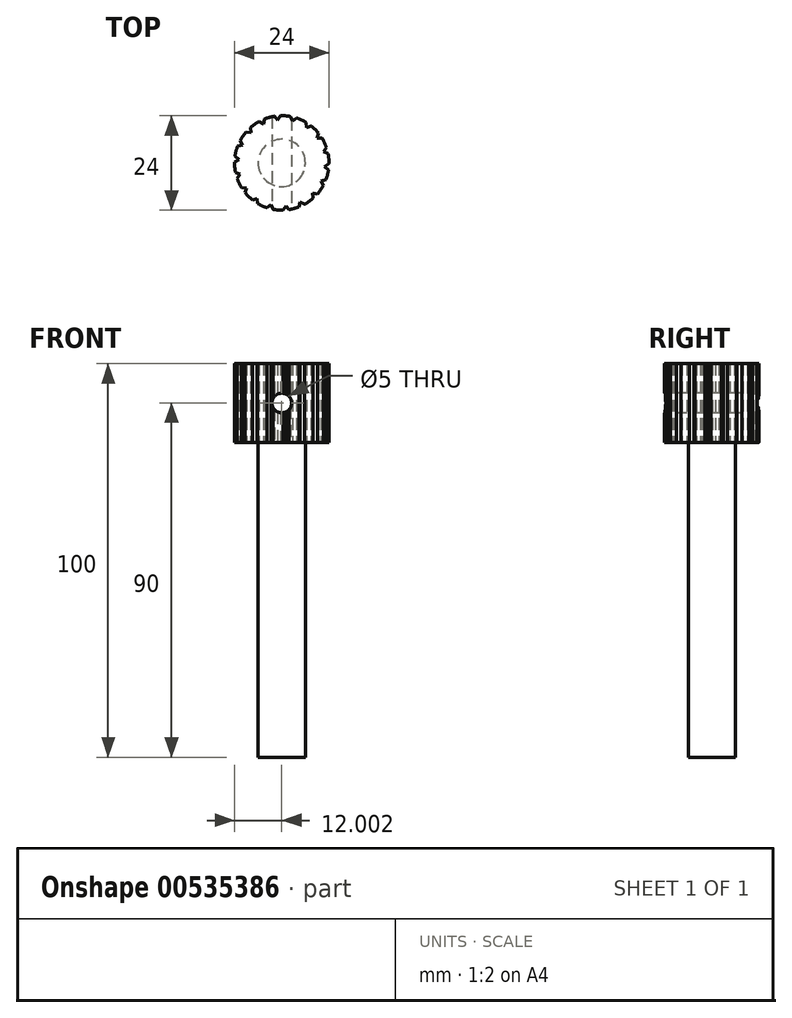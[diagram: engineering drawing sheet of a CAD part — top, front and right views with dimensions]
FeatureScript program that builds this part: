
annotation { "Feature Type Name" : "Feature", "Feature Type Description" : "" }
export const myFeature = defineFeature(function(context is Context, id is Id, definition is map)
    precondition{}
    {
        {
            var Q0;
            Q0=qCreatedBy(makeId("Top.planeOp"),FACE);
            var sketch = newSketch(context, id + "F0", { "sketchPlane" : qUnion([Q0])});
            skArc(sketch, "E0", {"start": v(-11.7, 21.75) * mm, "mid": v(-12.8, 21.05) * mm, "end": v(-13.83, 20.24) * mm});
            skLineSegment(sketch, "E1", {"start": v(-11.7, 21.75) * mm, "end": v(-10.55, 21.16) * mm});
            skLineSegment(sketch, "E2.MirrorCS", {"start": v(-10.28, 22.42) * mm, "end": v(-10.55, 21.16) * mm});
            skLineSegment(sketch, "E3.1.0", {"start": v(-13.83, 20.24) * mm, "end": v(-13.66, 18.96) * mm});
            skLineSegment(sketch, "E3.1.1", {"start": v(-14.94, 19.12) * mm, "end": v(-13.66, 18.96) * mm});
            skLineSegment(sketch, "E3.2.0", {"start": v(-16.42, 16.97) * mm, "end": v(-15.82, 15.83) * mm});
            skLineSegment(sketch, "E3.2.1", {"start": v(-17.08, 15.54) * mm, "end": v(-15.82, 15.83) * mm});
            skLineSegment(sketch, "E3.3.0", {"start": v(-17.74, 13.02) * mm, "end": v(-16.78, 12.15) * mm});
            skLineSegment(sketch, "E3.3.1", {"start": v(-17.87, 11.45) * mm, "end": v(-16.78, 12.15) * mm});
            skLineSegment(sketch, "E3.4.0", {"start": v(-17.62, 8.85) * mm, "end": v(-16.43, 8.37) * mm});
            skLineSegment(sketch, "E3.4.1", {"start": v(-17.2, 7.34) * mm, "end": v(-16.43, 8.37) * mm});
            skLineSegment(sketch, "E3.5.0", {"start": v(-16.1, 4.98) * mm, "end": v(-14.8, 4.93) * mm});
            skLineSegment(sketch, "E3.5.1", {"start": v(-15.18, 3.7) * mm, "end": v(-14.8, 4.93) * mm});
            skLineSegment(sketch, "E3.6.0", {"start": v(-13.33, 1.86) * mm, "end": v(-12.1, 2.25) * mm});
            skLineSegment(sketch, "E3.6.1", {"start": v(-12.03, 0.97) * mm, "end": v(-12.1, 2.25) * mm});
            skLineSegment(sketch, "E3.7.0", {"start": v(-9.66, -0.12) * mm, "end": v(-8.64, 0.67) * mm});
            skLineSegment(sketch, "E3.7.1", {"start": v(-8.14, -0.52) * mm, "end": v(-8.64, 0.67) * mm});
            skLineSegment(sketch, "E3.8.0", {"start": v(-5.54, -0.73) * mm, "end": v(-4.85, 0.36) * mm});
            skLineSegment(sketch, "E3.8.1", {"start": v(-3.97, -0.59) * mm, "end": v(-4.85, 0.36) * mm});
            skLineSegment(sketch, "E3.9.0", {"start": v(-1.46, 0.1) * mm, "end": v(-1.18, 1.36) * mm});
            skLineSegment(sketch, "E3.9.1", {"start": v(-0.03, 0.77) * mm, "end": v(-1.18, 1.36) * mm});
            skLineSegment(sketch, "E3.10.0", {"start": v(2.1, 2.28) * mm, "end": v(1.92, 3.56) * mm});
            skLineSegment(sketch, "E3.10.1", {"start": v(3.2, 3.4) * mm, "end": v(1.92, 3.56) * mm});
            skLineSegment(sketch, "E3.11.0", {"start": v(4.69, 5.55) * mm, "end": v(4.08, 6.7) * mm});
            skLineSegment(sketch, "E3.11.1", {"start": v(5.34, 6.98) * mm, "end": v(4.08, 6.7) * mm});
            skLineSegment(sketch, "E3.12.0", {"start": v(6, 9.5) * mm, "end": v(5.05, 10.37) * mm});
            skLineSegment(sketch, "E3.12.1", {"start": v(6.13, 11.07) * mm, "end": v(5.05, 10.37) * mm});
            skLineSegment(sketch, "E3.13.0", {"start": v(5.89, 13.67) * mm, "end": v(4.7, 14.16) * mm});
            skLineSegment(sketch, "E3.13.1", {"start": v(5.47, 15.18) * mm, "end": v(4.7, 14.16) * mm});
            skLineSegment(sketch, "E3.14.0", {"start": v(4.36, 17.54) * mm, "end": v(3.07, 17.6) * mm});
            skLineSegment(sketch, "E3.14.1", {"start": v(3.45, 18.83) * mm, "end": v(3.07, 17.6) * mm});
            skLineSegment(sketch, "E3.15.0", {"start": v(1.59, 20.66) * mm, "end": v(0.36, 20.27) * mm});
            skLineSegment(sketch, "E3.15.1", {"start": v(0.3, 21.56) * mm, "end": v(0.36, 20.27) * mm});
            skLineSegment(sketch, "E3.16.0", {"start": v(-2.08, 22.65) * mm, "end": v(-3.1, 21.86) * mm});
            skLineSegment(sketch, "E3.16.1", {"start": v(-3.6, 23.04) * mm, "end": v(-3.1, 21.86) * mm});
            skLineSegment(sketch, "E3.17.0", {"start": v(-6.2, 23.26) * mm, "end": v(-6.89, 22.17) * mm});
            skLineSegment(sketch, "E3.17.1", {"start": v(-7.76, 23.11) * mm, "end": v(-6.89, 22.17) * mm});
            skArc(sketch, "E4.trimOffspring", {"start": v(-14.94, 19.12) * mm, "mid": v(-15.74, 18.09) * mm, "end": v(-16.42, 16.97) * mm});
            skArc(sketch, "E5.trimOffspring", {"start": v(-17.08, 15.54) * mm, "mid": v(-17.48, 14.3) * mm, "end": v(-17.74, 13.02) * mm});
            skArc(sketch, "E6.trimOffspring", {"start": v(-17.87, 11.45) * mm, "mid": v(-17.82, 10.15) * mm, "end": v(-17.62, 8.85) * mm});
            skArc(sketch, "E7.trimOffspring", {"start": v(-17.2, 7.34) * mm, "mid": v(-16.71, 6.13) * mm, "end": v(-16.1, 4.98) * mm});
            skArc(sketch, "E8.trimOffspring", {"start": v(-15.18, 3.7) * mm, "mid": v(-14.3, 2.73) * mm, "end": v(-13.33, 1.86) * mm});
            skArc(sketch, "E9.trimOffspring", {"start": v(-12.03, 0.97) * mm, "mid": v(-10.88, 0.36) * mm, "end": v(-9.66, -0.12) * mm});
            skArc(sketch, "E10.trimOffspring", {"start": v(-8.14, -0.52) * mm, "mid": v(-6.85, -0.7) * mm, "end": v(-5.54, -0.73) * mm});
            skArc(sketch, "E11.trimOffspring", {"start": v(-3.97, -0.59) * mm, "mid": v(-2.7, -0.31) * mm, "end": v(-1.46, 0.1) * mm});
            skArc(sketch, "E12.trimOffspring", {"start": v(-0.03, 0.77) * mm, "mid": v(1.07, 1.47) * mm, "end": v(2.1, 2.28) * mm});
            skArc(sketch, "E13.trimOffspring", {"start": v(3.2, 3.4) * mm, "mid": v(4, 4.43) * mm, "end": v(4.69, 5.55) * mm});
            skArc(sketch, "E14.trimOffspring", {"start": v(5.34, 6.98) * mm, "mid": v(5.74, 8.22) * mm, "end": v(6, 9.5) * mm});
            skArc(sketch, "E15.trimOffspring", {"start": v(6.13, 11.07) * mm, "mid": v(6.08, 12.38) * mm, "end": v(5.89, 13.67) * mm});
            skArc(sketch, "E16.trimOffspring", {"start": v(5.47, 15.18) * mm, "mid": v(4.98, 16.4) * mm, "end": v(4.36, 17.54) * mm});
            skArc(sketch, "E17.trimOffspring", {"start": v(3.45, 18.83) * mm, "mid": v(2.57, 19.8) * mm, "end": v(1.59, 20.66) * mm});
            skArc(sketch, "E18.trimOffspring", {"start": v(0.3, 21.56) * mm, "mid": v(-0.86, 22.17) * mm, "end": v(-2.08, 22.65) * mm});
            skArc(sketch, "E19.trimOffspring", {"start": v(-3.6, 23.04) * mm, "mid": v(-4.9, 23.22) * mm, "end": v(-6.2, 23.26) * mm});
            skArc(sketch, "E20.trimOffspring", {"start": v(-7.76, 23.11) * mm, "mid": v(-9.04, 22.83) * mm, "end": v(-10.28, 22.42) * mm});
            skSolve(sketch);
        }
        {
            var Q0;
            Q0 = qSketchRegion(id + "F0", true);
            extrude(context, id + "F1", {"entities" : qUnion([Q0]), "depth" : 20 * mm, "offsetDistance" : 25 * mm});
        }
        {
            var Q0;
            Q0=qCreatedBy(makeId("Front.planeOp"),FACE);
            cPlane(context, id + "F2", {"entities" : qUnion([Q0]), "cplaneType" : CPlaneType.OFFSET, "offset" : 25 * mm, "width" : 150 * mm, "height" : 150 * mm});
        }
        {
            var Q0;
            Q0=qCreatedBy(id+"F2.planeOp",FACE);
            var sketch = newSketch(context, id + "F3", { "sketchPlane" : qUnion([Q0])});
            skCircle(sketch, "E21", {"center": v(-5.87, 10) * mm, "radius": 2.5 * mm});
            skSolve(sketch);
        }
        {
            var Q0;
            Q0=makeQuery(id+"F3.imprint","IMPRINT",FACE,{"disambiguationData":[TD([[makeQuery(id+"F3.imprint","IMPRINT",EDGE,{"derivedFrom":sQuery(id+"F3.wireOp",EDGE,"E21")}),1.0]])]});
            extrude(context, id + "F4", {"entities" : qUnion([Q0]), "operationType" : NewBodyOperationType.REMOVE, "endBound" : BoundingType.THROUGH_ALL, "oppositeDirection" : true, "depth" : 25 * mm, "offsetDistance" : 25 * mm});
        }
        {
            var Q0;
            Q0=makeQuery(id+"F1.opExtrude","CAP_FACE",FACE,{"disambiguationData":[OSD([sQuery(id+"F0.wireOp",EDGE,"E0"),sQuery(id+"F0.wireOp",EDGE,"E1"),sQuery(id+"F0.wireOp",EDGE,"E2.MirrorCS"),sQuery(id+"F0.wireOp",EDGE,"E3.1.0"),sQuery(id+"F0.wireOp",EDGE,"E3.1.1"),sQuery(id+"F0.wireOp",EDGE,"E3.2.0"),sQuery(id+"F0.wireOp",EDGE,"E3.2.1"),sQuery(id+"F0.wireOp",EDGE,"E3.3.0"),sQuery(id+"F0.wireOp",EDGE,"E3.3.1"),sQuery(id+"F0.wireOp",EDGE,"E3.4.0"),sQuery(id+"F0.wireOp",EDGE,"E3.4.1"),sQuery(id+"F0.wireOp",EDGE,"E3.5.0"),sQuery(id+"F0.wireOp",EDGE,"E3.5.1"),sQuery(id+"F0.wireOp",EDGE,"E3.6.0"),sQuery(id+"F0.wireOp",EDGE,"E3.6.1"),sQuery(id+"F0.wireOp",EDGE,"E3.7.0"),sQuery(id+"F0.wireOp",EDGE,"E3.7.1"),sQuery(id+"F0.wireOp",EDGE,"E3.8.0"),sQuery(id+"F0.wireOp",EDGE,"E3.8.1"),sQuery(id+"F0.wireOp",EDGE,"E3.9.0"),sQuery(id+"F0.wireOp",EDGE,"E3.9.1"),sQuery(id+"F0.wireOp",EDGE,"E3.10.0"),sQuery(id+"F0.wireOp",EDGE,"E3.10.1"),sQuery(id+"F0.wireOp",EDGE,"E3.11.0"),sQuery(id+"F0.wireOp",EDGE,"E3.11.1"),sQuery(id+"F0.wireOp",EDGE,"E3.12.0"),sQuery(id+"F0.wireOp",EDGE,"E3.12.1"),sQuery(id+"F0.wireOp",EDGE,"E3.13.0"),sQuery(id+"F0.wireOp",EDGE,"E3.13.1"),sQuery(id+"F0.wireOp",EDGE,"E3.14.0"),sQuery(id+"F0.wireOp",EDGE,"E3.14.1"),sQuery(id+"F0.wireOp",EDGE,"E3.15.0"),sQuery(id+"F0.wireOp",EDGE,"E3.15.1"),sQuery(id+"F0.wireOp",EDGE,"E3.16.0"),sQuery(id+"F0.wireOp",EDGE,"E3.16.1"),sQuery(id+"F0.wireOp",EDGE,"E3.17.0"),sQuery(id+"F0.wireOp",EDGE,"E3.17.1"),sQuery(id+"F0.wireOp",EDGE,"E4.trimOffspring"),sQuery(id+"F0.wireOp",EDGE,"E5.trimOffspring"),sQuery(id+"F0.wireOp",EDGE,"E6.trimOffspring"),sQuery(id+"F0.wireOp",EDGE,"E7.trimOffspring"),sQuery(id+"F0.wireOp",EDGE,"E8.trimOffspring"),sQuery(id+"F0.wireOp",EDGE,"E9.trimOffspring"),sQuery(id+"F0.wireOp",EDGE,"E10.trimOffspring"),sQuery(id+"F0.wireOp",EDGE,"E11.trimOffspring"),sQuery(id+"F0.wireOp",EDGE,"E12.trimOffspring"),sQuery(id+"F0.wireOp",EDGE,"E13.trimOffspring"),sQuery(id+"F0.wireOp",EDGE,"E14.trimOffspring"),sQuery(id+"F0.wireOp",EDGE,"E15.trimOffspring"),sQuery(id+"F0.wireOp",EDGE,"E16.trimOffspring"),sQuery(id+"F0.wireOp",EDGE,"E17.trimOffspring"),sQuery(id+"F0.wireOp",EDGE,"E18.trimOffspring"),sQuery(id+"F0.wireOp",EDGE,"E19.trimOffspring"),sQuery(id+"F0.wireOp",EDGE,"E20.trimOffspring")])],"isStart":true});
            var sketch = newSketch(context, id + "F5", { "sketchPlane" : qUnion([Q0])});
            skCircle(sketch, "E22", {"center": v(-5.87, -11.26) * mm, "radius": 6 * mm});
            skSolve(sketch);
        }
        {
            var Q0;
            Q0=makeQuery(id+"F5.imprint","IMPRINT",FACE,{"disambiguationData":[TD([[makeQuery(id+"F5.imprint","IMPRINT",EDGE,{"derivedFrom":sQuery(id+"F5.wireOp",EDGE,"E22")}),1.0]])]});
            extrude(context, id + "F6", {"entities" : qUnion([Q0]), "operationType" : NewBodyOperationType.ADD, "depth" : 80 * mm, "offsetDistance" : 25 * mm});
        }
    });
